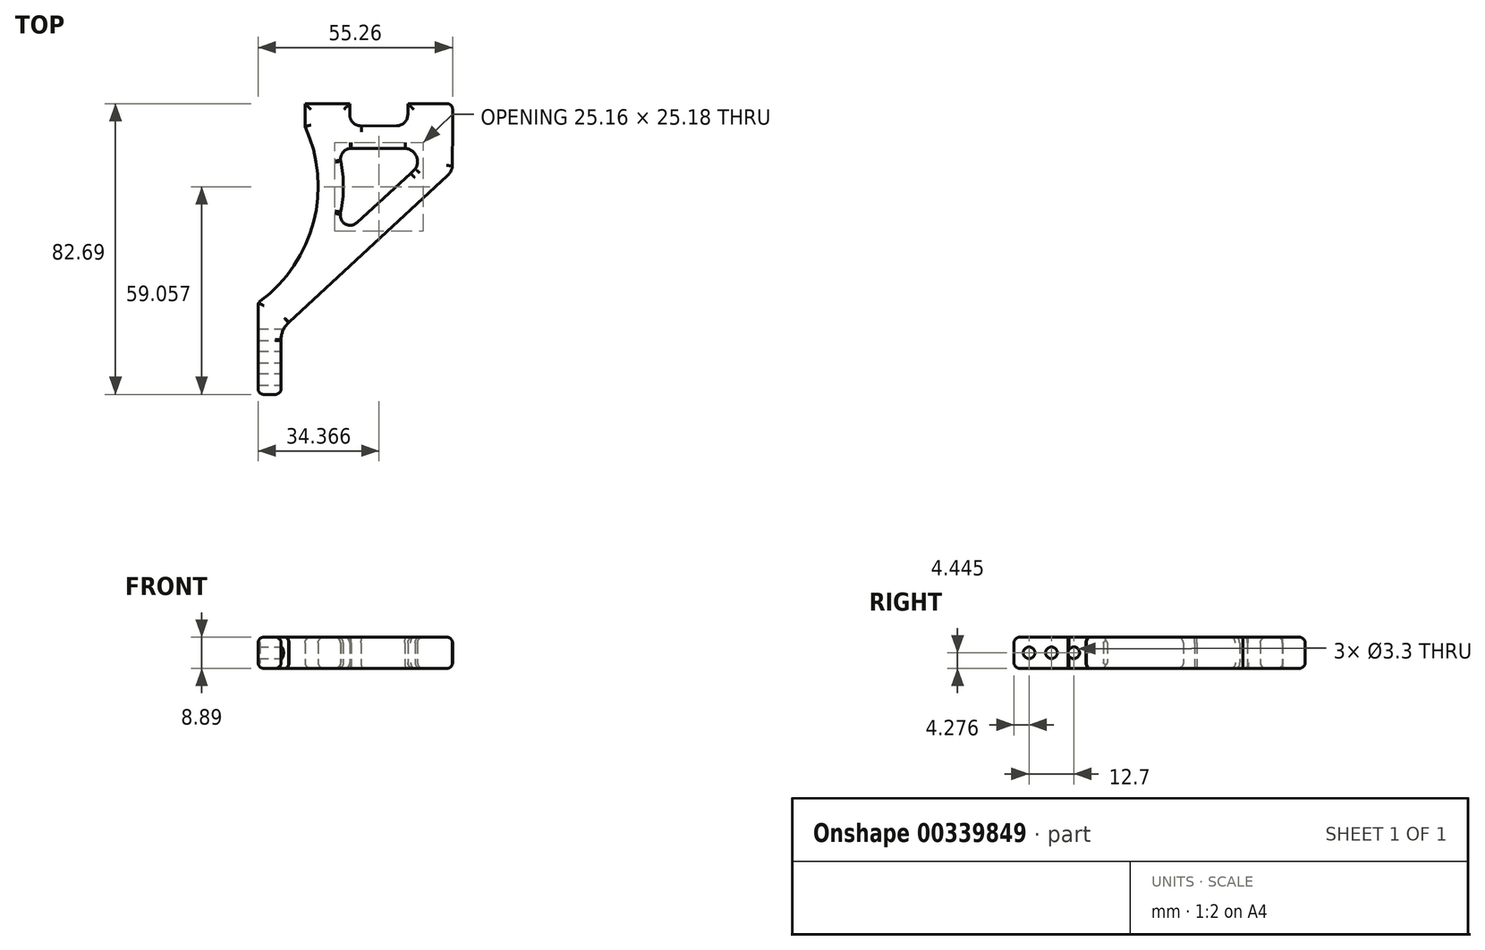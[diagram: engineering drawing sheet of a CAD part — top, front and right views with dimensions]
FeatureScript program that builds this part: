
annotation { "Feature Type Name" : "Feature", "Feature Type Description" : "" }
export const myFeature = defineFeature(function(context is Context, id is Id, definition is map)
    precondition{}
    {
        {
            var Q0;
            Q0=qCreatedBy(makeId("Top.planeOp"),FACE);
            var sketch = newSketch(context, id + "F0", { "sketchPlane" : qUnion([Q0])});
            skLineSegment(sketch, "E0.left", {"start": v(41.9, 22.85) * mm, "end": v(41.9, 16.36) * mm});
            skLineSegment(sketch, "E1.right", {"start": v(0, 22.82) * mm, "end": v(0, 16.36) * mm});
            skPoint(sketch, "E2", {"position": v(-13.35, -35.94) * mm});
            skLineSegment(sketch, "E3", {"start": v(30.03, 3.02) * mm, "end": v(31.32, 4.22) * mm});
            skArc(sketch, "E4", {"start": v(31.32, 4.22) * mm, "mid": v(31.58, 8.03) * mm, "end": v(28.41, 10.15) * mm});
            skArc(sketch, "E5", {"start": v(40.43, 2.3) * mm, "mid": v(41.62, 4.09) * mm, "end": v(41.88, 6.22) * mm});
            skLineSegment(sketch, "E6", {"start": v(41.9, 16.36) * mm, "end": v(41.88, 5.14) * mm});
            skLineSegment(sketch, "E7", {"start": v(40.43, 2.3) * mm, "end": v(-4.5, -39.3) * mm});
            skArc(sketch, "E8", {"start": v(26.03, 16.53) * mm, "mid": v(28.27, 17.46) * mm, "end": v(29.2, 19.7) * mm});
            skArc(sketch, "E9", {"start": v(12.72, 19.67) * mm, "mid": v(13.68, 17.4) * mm, "end": v(15.98, 16.5) * mm});
            skLineSegment(sketch, "E10", {"start": v(15.83, 16.5) * mm, "end": v(26.03, 16.53) * mm});
            skLineSegment(sketch, "E11", {"start": v(12.71, 22.85) * mm, "end": v(12.72, 19.67) * mm});
            skLineSegment(sketch, "E12", {"start": v(29.2, 22.85) * mm, "end": v(29.2, 19.7) * mm});
            skLineSegment(sketch, "E13", {"start": v(-6.79, -44.55) * mm, "end": v(-6.79, -58.18) * mm});
            skLineSegment(sketch, "E14", {"start": v(-8.44, -59.84) * mm, "end": v(-11.7, -59.84) * mm});
            skLineSegment(sketch, "E15", {"start": v(-13.35, -58.18) * mm, "end": v(-13.35, -34.41) * mm});
            skArc(sketch, "E16", {"start": v(-12.82, -33.37) * mm, "mid": v(2.45, -10.79) * mm, "end": v(0, 16.36) * mm});
            skPoint(sketch, "E17", {"position": v(6.3, 16.47) * mm});
            skArc(sketch, "E18", {"start": v(10.13, -7.94) * mm, "mid": v(10.89, -0.76) * mm, "end": v(10.14, 6.43) * mm});
            skLineSegment(sketch, "E19", {"start": v(28.41, 10.15) * mm, "end": v(13.18, 10.15) * mm});
            skArc(sketch, "E20", {"start": v(10.08, -8.6) * mm, "mid": v(11.55, -11.45) * mm, "end": v(14.72, -11.03) * mm});
            skLineSegment(sketch, "E21", {"start": v(30.03, 3.02) * mm, "end": v(14.72, -11.03) * mm});
            skLineSegment(sketch, "E22", {"start": v(10.13, -7.94) * mm, "end": v(10.08, -8.6) * mm});
            skArc(sketch, "E23", {"start": v(12.95, 10.13) * mm, "mid": v(10.81, 9.02) * mm, "end": v(10.11, 6.7) * mm});
            skLineSegment(sketch, "E24", {"start": v(10.1, 6.75) * mm, "end": v(10.14, 6.43) * mm});
            skLineSegment(sketch, "E25", {"start": v(13.18, 10.15) * mm, "end": v(12.95, 10.13) * mm});
            skArc(sketch, "E26", {"start": v(-4.62, -39.43) * mm, "mid": v(-6.25, -41.6) * mm, "end": v(-6.76, -44.28) * mm});
            skLineSegment(sketch, "E27", {"start": v(-4.5, -39.3) * mm, "end": v(-4.62, -39.43) * mm});
            skLineSegment(sketch, "E28", {"start": v(-6.79, -44.55) * mm, "end": v(-6.76, -44.28) * mm});
            skArc(sketch, "E29", {"start": v(-12.49, -33.12) * mm, "mid": v(-13.18, -33.85) * mm, "end": v(-13.35, -34.84) * mm});
            skPoint(sketch, "E30", {"position": v(3.18, 25.94) * mm});
            skPoint(sketch, "E31", {"position": v(9.55, 25.94) * mm});
            skPoint(sketch, "E32", {"position": v(32.36, 25.94) * mm});
            skPoint(sketch, "E33", {"position": v(38.73, 25.96) * mm});
            skPoint(sketch, "E34.visualSharp", {"position": v(-6.79, -59.84) * mm});
            skArc(sketch, "E34.filletArc", {"start": v(-8.44, -59.84) * mm, "mid": v(-7.27, -59.35) * mm, "end": v(-6.79, -58.18) * mm});
            skPoint(sketch, "E35.visualSharp", {"position": v(-13.35, -59.84) * mm});
            skArc(sketch, "E35.filletArc", {"start": v(-13.35, -58.18) * mm, "mid": v(-12.87, -59.35) * mm, "end": v(-11.7, -59.84) * mm});
            skLineSegment(sketch, "E36", {"start": v(0, 22.82) * mm, "end": v(12.71, 22.85) * mm});
            skLineSegment(sketch, "E37", {"start": v(29.2, 22.85) * mm, "end": v(41.9, 22.85) * mm});
            skSolve(sketch);
        }
        {
            var Q0;
            Q0=makeQuery(id+"F0.imprint","IMPRINT",FACE,{"disambiguationData":[TD([[makeQuery(id+"F0.imprint","IMPRINT",EDGE,{"derivedFrom":sQuery(id+"F0.wireOp",EDGE,"E0.left")}),-1.0]])]});
            extrude(context, id + "F1", {"entities" : qUnion([Q0]), "depth" : 8.9 * mm});
        }
        {
            var Q0;
            Q0=makeQuery(id+"F1.opExtrude","CAP_EDGE",EDGE,{"disambiguationData":[OSD([sQuery(id+"F0.wireOp",EDGE,"E0.left")])],"isStart":false});
            var Q1;
            Q1=makeQuery(id+"F1.opExtrude","CAP_FACE",FACE,{"disambiguationData":[OSD([sQuery(id+"F0.wireOp",EDGE,"YZ92rBNX-Mz95-2knB-doQ8-QHTFhwNA1oBr.bottom"),sQuery(id+"F0.wireOp",EDGE,"E0.bottom"),sQuery(id+"F0.wireOp",EDGE,"E0.left"),sQuery(id+"F0.wireOp",EDGE,"E1.right"),sQuery(id+"F0.wireOp",EDGE,"SzI1FcWJ-gVPU-Ooe5-hQlX-CRs42xu8LLNW"),sQuery(id+"F0.wireOp",EDGE,"TPr3rdG5-SIDz-w58Y-6eqx-M6IK6jSWFhIM"),sQuery(id+"F0.wireOp",EDGE,"noc51GMV-Ahoo-WSD5-Lxts-qJhaJEb6VlAm"),sQuery(id+"F0.wireOp",EDGE,"E3FnssW3-ZQiV-QDWY-5dQY-6bhZWmJ5cOBN"),sQuery(id+"F0.wireOp",EDGE,"cVz8xXeH-HXYV-y1n5-9CkQ-8dIsYkVWRJSO"),sQuery(id+"F0.wireOp",EDGE,"E3"),sQuery(id+"F0.wireOp",EDGE,"E4"),sQuery(id+"F0.wireOp",EDGE,"ISvdj8wT-oJ9k-pktH-wGl1-ypRnDfL9eN0U"),sQuery(id+"F0.wireOp",EDGE,"9vAMhoP7-wnIn-WaFN-PusH-oHm1aDkgCJVd"),sQuery(id+"F0.wireOp",EDGE,"Jhohd9hE-lPSl-7JDe-2Hk6-lUpt38s9H9Yq"),sQuery(id+"F0.wireOp",EDGE,"kMEoYta0-bXeg-MWsG-sC0e-sf47EgIndYf1"),sQuery(id+"F0.wireOp",EDGE,"G2y1UMqk-i9hO-i7C4-I75O-fc8mSGVlh6aF"),sQuery(id+"F0.wireOp",EDGE,"E5"),sQuery(id+"F0.wireOp",EDGE,"E6"),sQuery(id+"F0.wireOp",EDGE,"3kRvRCZS-lmxn-bb7c-7CfW-55qZRIPDTbnd"),sQuery(id+"F0.wireOp",EDGE,"iQ2rey6d-C9uf-Z5wj-gwGX-4HWEF9hhR8Rk"),sQuery(id+"F0.wireOp",EDGE,"E7"),sQuery(id+"F0.wireOp",EDGE,"EIM5bmiI-A2SF-qGVZ-bvCF-VrnpqsO6tJdX"),sQuery(id+"F0.wireOp",EDGE,"ilSpvZOG-ijNh-z112-y927-mz7fLowJOJxK"),sQuery(id+"F0.wireOp",EDGE,"El7EWY2H-2ioG-ogYt-Owtm-aVWLtx5Oh5om"),sQuery(id+"F0.wireOp",EDGE,"dyHQTCYp-uGCR-qaTb-hvYm-Fg8xv5Bd20ul"),sQuery(id+"F0.wireOp",EDGE,"kbVTQr7z-w13S-F5we-hJcG-RMuXYoLscjPo"),sQuery(id+"F0.wireOp",EDGE,"E8"),sQuery(id+"F0.wireOp",EDGE,"E9"),sQuery(id+"F0.wireOp",EDGE,"E10"),sQuery(id+"F0.wireOp",EDGE,"E11"),sQuery(id+"F0.wireOp",EDGE,"E12"),sQuery(id+"F0.wireOp",EDGE,"5bf2f562-2b39-48da-8c70-fd73b6cb9478.filletArc"),sQuery(id+"F0.wireOp",EDGE,"813d53ed-6ea3-4024-ad01-9081af5508ea.filletArc"),sQuery(id+"F0.wireOp",EDGE,"201358cc-a45b-47bb-b463-8872e7bce510.filletArc")])],"isStart":false});
            var Q2;
            Q2=makeQuery(id+"F1.opExtrude","CAP_FACE",FACE,{"disambiguationData":[OSD([sQuery(id+"F0.wireOp",EDGE,"YZ92rBNX-Mz95-2knB-doQ8-QHTFhwNA1oBr.bottom"),sQuery(id+"F0.wireOp",EDGE,"E0.bottom"),sQuery(id+"F0.wireOp",EDGE,"E0.left"),sQuery(id+"F0.wireOp",EDGE,"E1.right"),sQuery(id+"F0.wireOp",EDGE,"SzI1FcWJ-gVPU-Ooe5-hQlX-CRs42xu8LLNW"),sQuery(id+"F0.wireOp",EDGE,"TPr3rdG5-SIDz-w58Y-6eqx-M6IK6jSWFhIM"),sQuery(id+"F0.wireOp",EDGE,"noc51GMV-Ahoo-WSD5-Lxts-qJhaJEb6VlAm"),sQuery(id+"F0.wireOp",EDGE,"E3FnssW3-ZQiV-QDWY-5dQY-6bhZWmJ5cOBN"),sQuery(id+"F0.wireOp",EDGE,"cVz8xXeH-HXYV-y1n5-9CkQ-8dIsYkVWRJSO"),sQuery(id+"F0.wireOp",EDGE,"E3"),sQuery(id+"F0.wireOp",EDGE,"E4"),sQuery(id+"F0.wireOp",EDGE,"ISvdj8wT-oJ9k-pktH-wGl1-ypRnDfL9eN0U"),sQuery(id+"F0.wireOp",EDGE,"9vAMhoP7-wnIn-WaFN-PusH-oHm1aDkgCJVd"),sQuery(id+"F0.wireOp",EDGE,"Jhohd9hE-lPSl-7JDe-2Hk6-lUpt38s9H9Yq"),sQuery(id+"F0.wireOp",EDGE,"kMEoYta0-bXeg-MWsG-sC0e-sf47EgIndYf1"),sQuery(id+"F0.wireOp",EDGE,"G2y1UMqk-i9hO-i7C4-I75O-fc8mSGVlh6aF"),sQuery(id+"F0.wireOp",EDGE,"E5"),sQuery(id+"F0.wireOp",EDGE,"E6"),sQuery(id+"F0.wireOp",EDGE,"3kRvRCZS-lmxn-bb7c-7CfW-55qZRIPDTbnd"),sQuery(id+"F0.wireOp",EDGE,"iQ2rey6d-C9uf-Z5wj-gwGX-4HWEF9hhR8Rk"),sQuery(id+"F0.wireOp",EDGE,"E7"),sQuery(id+"F0.wireOp",EDGE,"EIM5bmiI-A2SF-qGVZ-bvCF-VrnpqsO6tJdX"),sQuery(id+"F0.wireOp",EDGE,"ilSpvZOG-ijNh-z112-y927-mz7fLowJOJxK"),sQuery(id+"F0.wireOp",EDGE,"El7EWY2H-2ioG-ogYt-Owtm-aVWLtx5Oh5om"),sQuery(id+"F0.wireOp",EDGE,"dyHQTCYp-uGCR-qaTb-hvYm-Fg8xv5Bd20ul"),sQuery(id+"F0.wireOp",EDGE,"kbVTQr7z-w13S-F5we-hJcG-RMuXYoLscjPo"),sQuery(id+"F0.wireOp",EDGE,"E8"),sQuery(id+"F0.wireOp",EDGE,"E9"),sQuery(id+"F0.wireOp",EDGE,"E10"),sQuery(id+"F0.wireOp",EDGE,"E11"),sQuery(id+"F0.wireOp",EDGE,"E12"),sQuery(id+"F0.wireOp",EDGE,"5bf2f562-2b39-48da-8c70-fd73b6cb9478.filletArc"),sQuery(id+"F0.wireOp",EDGE,"813d53ed-6ea3-4024-ad01-9081af5508ea.filletArc"),sQuery(id+"F0.wireOp",EDGE,"201358cc-a45b-47bb-b463-8872e7bce510.filletArc")])],"isStart":true});
            var Q3;
            Q3=makeQuery(id+"F1.opExtrude","SWEPT_EDGE",EDGE,{"disambiguationData":[OSD([sQuery(id+"F0.wireOp",EDGE,"E0.bottom"),sQuery(id+"F0.wireOp",EDGE,"E0.left")])]});
            var Q4;
            Q4=makeQuery(id+"F1.opExtrude","SWEPT_EDGE",EDGE,{"disambiguationData":[OSD([sQuery(id+"F0.wireOp",EDGE,"noc51GMV-Ahoo-WSD5-Lxts-qJhaJEb6VlAm"),sQuery(id+"F0.wireOp",EDGE,"E3FnssW3-ZQiV-QDWY-5dQY-6bhZWmJ5cOBN")])]});
            var Q5;
            Q5=makeQuery(id+"F1.opExtrude","SWEPT_EDGE",EDGE,{"disambiguationData":[OSD([sQuery(id+"F0.wireOp",EDGE,"TPr3rdG5-SIDz-w58Y-6eqx-M6IK6jSWFhIM"),sQuery(id+"F0.wireOp",EDGE,"noc51GMV-Ahoo-WSD5-Lxts-qJhaJEb6VlAm")])]});
            fillet(context, id + "F2", {"entities" : qUnion([Q0, Q1, Q2, Q3, Q4, Q5]), "radius" : 1.65 * mm, "tangentPropagation" : true, "allowEdgeOverflow" : false});
        }
        {
            var Q0;
            Q0=makeQuery(id+"F1.opExtrude","SWEPT_FACE",FACE,{"disambiguationData":[OSD([sQuery(id+"F0.wireOp",EDGE,"E15")])]});
            var sketch = newSketch(context, id + "F3", { "sketchPlane" : qUnion([Q0])});
            skPoint(sketch, "E38", {"position": v(46.3, 7.24) * mm});
            skPoint(sketch, "E39", {"position": v(46.3, 1.65) * mm});
            skPoint(sketch, "E40", {"position": v(58.18, 4.45) * mm});
            skPoint(sketch, "E41", {"position": v(34.41, 4.45) * mm});
            skCircle(sketch, "E42", {"center": v(55.56, 4.45) * mm, "radius": 2.2 * mm});
            skPoint(sketch, "E43.orphan", {"position": v(34.41, 1.65) * mm});
            skPoint(sketch, "E44.orphan", {"position": v(58.18, 1.65) * mm});
            skLineSegment(sketch, "E45", {"start": v(58.18, 4.45) * mm, "end": v(34.41, 4.45) * mm});
            skCircle(sketch, "E46", {"center": v(42.86, 4.45) * mm, "radius": 2.15 * mm});
            skCircle(sketch, "E47", {"center": v(49.21, 4.45) * mm, "radius": 2.1 * mm});
            skSolve(sketch);
        }
        {
            var Q0;
            Q0=sQuery(id+"F3.wireOp",VERTEX,"E42.center");
            var Q1;
            Q1=sQuery(id+"F3.wireOp",VERTEX,"E47.center");
            var Q2;
            Q2=sQuery(id+"F3.wireOp",VERTEX,"E46.center");
            var Q3;
            Q3=makeQuery(id+"F1.opExtrude","SWEPT_BODY",BODY,{"disambiguationData":[OSD([sQuery(id+"F0.wireOp",EDGE,"E0.left"),sQuery(id+"F0.wireOp",EDGE,"E1.right"),sQuery(id+"F0.wireOp",EDGE,"E3"),sQuery(id+"F0.wireOp",EDGE,"E4"),sQuery(id+"F0.wireOp",EDGE,"E5"),sQuery(id+"F0.wireOp",EDGE,"E6"),sQuery(id+"F0.wireOp",EDGE,"E7"),sQuery(id+"F0.wireOp",EDGE,"E8"),sQuery(id+"F0.wireOp",EDGE,"E9"),sQuery(id+"F0.wireOp",EDGE,"E10"),sQuery(id+"F0.wireOp",EDGE,"E11"),sQuery(id+"F0.wireOp",EDGE,"E12"),sQuery(id+"F0.wireOp",EDGE,"E13"),sQuery(id+"F0.wireOp",EDGE,"E14"),sQuery(id+"F0.wireOp",EDGE,"E15"),sQuery(id+"F0.wireOp",EDGE,"E16"),sQuery(id+"F0.wireOp",EDGE,"E18"),sQuery(id+"F0.wireOp",EDGE,"E19"),sQuery(id+"F0.wireOp",EDGE,"E20"),sQuery(id+"F0.wireOp",EDGE,"E21"),sQuery(id+"F0.wireOp",EDGE,"E22"),sQuery(id+"F0.wireOp",EDGE,"E23"),sQuery(id+"F0.wireOp",EDGE,"E24"),sQuery(id+"F0.wireOp",EDGE,"E25"),sQuery(id+"F0.wireOp",EDGE,"E26"),sQuery(id+"F0.wireOp",EDGE,"E27"),sQuery(id+"F0.wireOp",EDGE,"E28"),sQuery(id+"F0.wireOp",EDGE,"E29"),sQuery(id+"F0.wireOp",EDGE,"181tW4vp-ZbtW-davR-69ns-0IIxqZoocxi7"),sQuery(id+"F0.wireOp",EDGE,"CLDTVJRU-Zfvq-rIZ4-dqXF-aQIPlVdSOrB2"),sQuery(id+"F0.wireOp",EDGE,"2JWichqw-htUA-xdmc-76uD-T1Hjylxb60dA"),sQuery(id+"F0.wireOp",EDGE,"FRX9JyIv-8L25-IehD-1VqH-pjbuIYerUjMn"),sQuery(id+"F0.wireOp",EDGE,"0ZqjfKFE-V8Ua-lY5Q-Bvau-9FpRgLLehYvd"),sQuery(id+"F0.wireOp",EDGE,"Xe9JL77E-bn8W-FsuT-8ZNO-0icE26lyWPuJ"),sQuery(id+"F0.wireOp",EDGE,"E34.filletArc"),sQuery(id+"F0.wireOp",EDGE,"E35.filletArc")])]});
            hole(context, id + "F4", {"style" : HoleStyle.SIMPLE, "endStyle" : HoleEndStyle.THROUGH, "standardTappedOrClearance" : lookupTablePath({ "standard" : "ISO", "fit" : "Normal", "size" : "M3", "type" : "Clearance" }), "standardBlindInLast" : lookupTablePath({ "fit" : "Standard", "standard" : "ISO", "size" : "M3", "type" : "Clearance" }), "holeDiameter" : 3.3 * mm, "isTappedThrough" : true, "tappedDepth" : 12.7 * mm, "tapClearance" : 3, "locations" : qUnion([Q0, Q1, Q2]), "scope" : qUnion([Q3]), "startStyle" : HoleStartStyle.PART});
        }
    });
